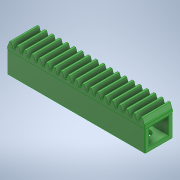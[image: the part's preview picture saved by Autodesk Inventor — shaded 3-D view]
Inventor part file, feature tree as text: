
AUTODESK INVENTOR PART (.ipt)
format: ipt  version: 2020 (Build 240168000, 168)  size: 599,040 bytes
history: native  units: in
note: dims shown in document units (in); Inventor stores cm internally (conversion verified against a paired STEP export)
features: fillet x1
ambient origin geometry x8: Origin, YZ Plane, XZ Plane, XY Plane, X Axis, Y Axis, Z Axis, Center Point
bodies: Solid1 (feature_tree)
feature tree (1):
  fillet  "Fillet11"  [1 undecoded]
note: 1 required parameter value undecoded (feature->parameter linkage not recoverable at this tier; creation-order binding heuristic only, values carry confidence <= 0.55)
